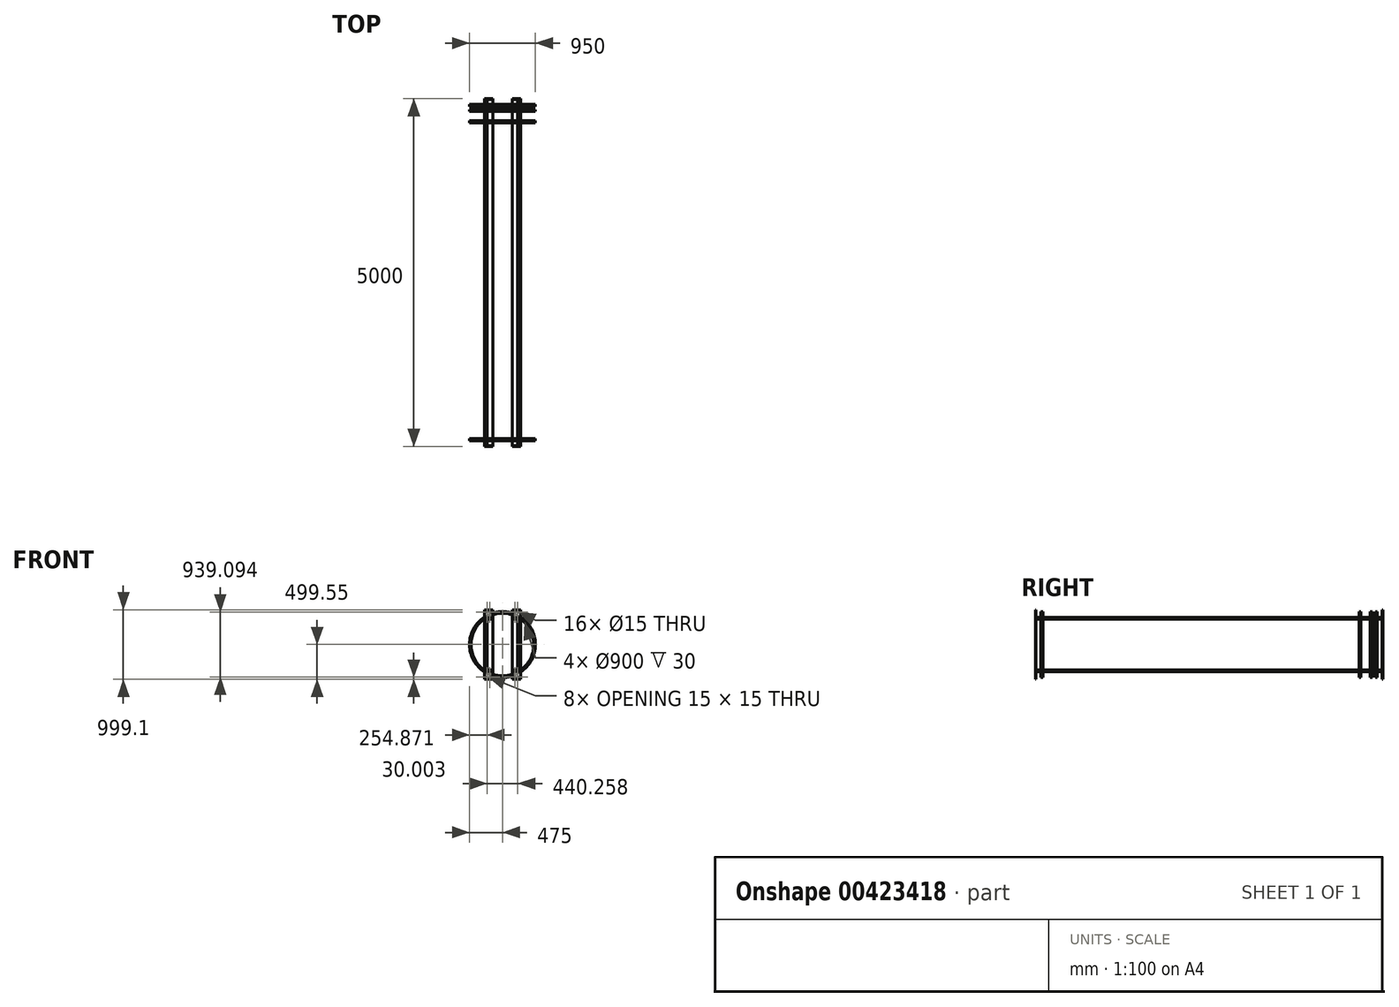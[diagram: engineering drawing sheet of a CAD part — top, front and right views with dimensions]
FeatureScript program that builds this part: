
annotation { "Feature Type Name" : "Feature", "Feature Type Description" : "" }
export const myFeature = defineFeature(function(context is Context, id is Id, definition is map)
    precondition{}
    {
        {
            var Q0;
            Q0=qCreatedBy(makeId("Front.planeOp"),FACE);
            var sketch = newSketch(context, id + "F0", { "sketchPlane" : qUnion([Q0])});
            skCircle(sketch, "E0", {"center": v(0, 0) * mm, "radius": 450 * mm, "construction": true});
            skLineSegment(sketch, "E1", {"start": v(0, 0) * mm, "end": v(0, 450) * mm, "construction": true});
            skLineSegment(sketch, "E2", {"start": v(0, 0) * mm, "end": v(-450, 0) * mm, "construction": true});
            skPoint(sketch, "E3", {"position": v(-236, 0) * mm});
            skPoint(sketch, "E4", {"position": v(-220, 0) * mm});
            skLineSegment(sketch, "E5", {"start": v(-236, 383.15) * mm, "end": v(-236, -383.15) * mm});
            skLineSegment(sketch, "E6", {"start": v(-220, 392.56) * mm, "end": v(-220, -392.56) * mm});
            skArc(sketch, "E7", {"start": v(-220, -392.56) * mm, "mid": v(-228.05, -387.94) * mm, "end": v(-236, -383.15) * mm});
            skLineSegment(sketch, "E8", {"start": v(-220, 383.15) * mm, "end": v(-140, 383.15) * mm});
            skLineSegment(sketch, "E9", {"start": v(-140, 383.15) * mm, "end": v(-140, 367.15) * mm});
            skLineSegment(sketch, "E10", {"start": v(-140, 367.15) * mm, "end": v(-220, 367.15) * mm});
            skLineSegment(sketch, "E11", {"start": v(-220, -383.15) * mm, "end": v(-140, -383.15) * mm});
            skLineSegment(sketch, "E12", {"start": v(-140, -383.15) * mm, "end": v(-140, -367.15) * mm});
            skLineSegment(sketch, "E13", {"start": v(-140, -367.15) * mm, "end": v(-220, -367.15) * mm});
            skPoint(sketch, "E14", {"position": v(-236, 383.15) * mm});
            skPoint(sketch, "E15", {"position": v(-220, 392.56) * mm});
            skLineSegment(sketch, "E16", {"start": v(-236, 367.15) * mm, "end": v(-260.2, 367.15) * mm});
            skArc(sketch, "E17", {"start": v(-220, 392.56) * mm, "mid": v(-240.43, 380.38) * mm, "end": v(-260.2, 367.15) * mm});
            skLineSegment(sketch, "E18", {"start": v(-236, -367.15) * mm, "end": v(-260.2, -367.15) * mm});
            skArc(sketch, "E19", {"start": v(-260.2, -367.15) * mm, "mid": v(-240.43, -380.38) * mm, "end": v(-220, -392.56) * mm});
            skArc(sketch, "E20.MirrorCS", {"start": v(220, -392.56) * mm, "mid": v(228.05, -387.94) * mm, "end": v(236, -383.15) * mm});
            skArc(sketch, "E21.MirrorCS", {"start": v(220, 392.56) * mm, "mid": v(240.43, 380.38) * mm, "end": v(260.2, 367.15) * mm});
            skLineSegment(sketch, "E22.MirrorCS", {"start": v(236, -367.15) * mm, "end": v(260.2, -367.15) * mm});
            skArc(sketch, "E23.MirrorCS", {"start": v(260.2, -367.15) * mm, "mid": v(240.43, -380.38) * mm, "end": v(220, -392.56) * mm});
            skLineSegment(sketch, "E24.MirrorCS", {"start": v(140, 383.15) * mm, "end": v(140, 367.15) * mm});
            skLineSegment(sketch, "E25.MirrorCS", {"start": v(140, -383.15) * mm, "end": v(140, -367.15) * mm});
            skLineSegment(sketch, "E26.MirrorCS", {"start": v(236, 367.15) * mm, "end": v(260.2, 367.15) * mm});
            skLineSegment(sketch, "E27.MirrorCS", {"start": v(236, 383.15) * mm, "end": v(236, -383.15) * mm});
            skPoint(sketch, "E28.MirrorP", {"position": v(220, 392.56) * mm});
            skLineSegment(sketch, "E29.MirrorCS", {"start": v(220, 392.56) * mm, "end": v(220, -392.56) * mm});
            skPoint(sketch, "E30.MirrorP", {"position": v(236, 0) * mm});
            skPoint(sketch, "E31.MirrorP", {"position": v(236, 383.15) * mm});
            skLineSegment(sketch, "E32.MirrorCS", {"start": v(220, -383.15) * mm, "end": v(140, -383.15) * mm});
            skLineSegment(sketch, "E33.MirrorCS", {"start": v(220, 383.15) * mm, "end": v(140, 383.15) * mm});
            skPoint(sketch, "E34.MirrorP", {"position": v(220, 0) * mm});
            skLineSegment(sketch, "E35.MirrorCS", {"start": v(140, -367.15) * mm, "end": v(220, -367.15) * mm});
            skLineSegment(sketch, "E36.MirrorCS", {"start": v(140, 367.15) * mm, "end": v(220, 367.15) * mm});
            skSolve(sketch);
        }
        {
            var Q0;
            Q0=makeQuery(id+"F0.imprint","IMPRINT",FACE,{"disambiguationData":[TD([[makeQuery(id+"F0.imprint","IMPRINT",EDGE,{"derivedFrom":sQuery(id+"F0.wireOp",EDGE,"E5")}),1.0]])]});
            var Q1;
            Q1=makeQuery(id+"F0.imprint","IMPRINT",FACE,{"disambiguationData":[TD([[makeQuery(id+"F0.imprint","IMPRINT",EDGE,{"derivedFrom":sQuery(id+"F0.wireOp",EDGE,"2efd4ff9-453e-46e9-b396-3085977d25950.MirrorCS")}),1.0]])]});
            var Q2;
            {var subQ3=sQuery(id+"F0.wireOp",EDGE,"E16");Q2=makeQuery(id+"F0.imprint","IMPRINT",FACE,{"disambiguationData":[TD([[makeQuery(id+"F0.imprint","IMPRINT",EDGE,{"derivedFrom":subQ3}),-1.0]])]});}
            var Q3;
            {var subQ0=sQuery(id+"F0.wireOp",EDGE,"E8");Q3=makeQuery(id+"F0.imprint","IMPRINT",FACE,{"disambiguationData":[TD([[makeQuery(id+"F0.imprint","IMPRINT",EDGE,{"derivedFrom":subQ0}),-1.0]])]});}
            var Q4;
            Q4=makeQuery(id+"F0.imprint","IMPRINT",FACE,{"disambiguationData":[TD([[makeQuery(id+"F0.imprint","IMPRINT",EDGE,{"derivedFrom":sQuery(id+"F0.wireOp",EDGE,"E24.MirrorCS")}),1.0]])]});
            var Q5;
            {var subQ0=sQuery(id+"F0.wireOp",EDGE,"E26.MirrorCS");Q5=makeQuery(id+"F0.imprint","IMPRINT",FACE,{"disambiguationData":[TD([[makeQuery(id+"F0.imprint","IMPRINT",EDGE,{"derivedFrom":subQ0}),1.0]])]});}
            var Q6;
            {var subQ2=sQuery(id+"F0.wireOp",EDGE,"E21.MirrorCS");var subQ5=sQuery(id+"F0.wireOp",EDGE,"E29.MirrorCS");var subQ10=makeQuery(id+"F0.imprint","INTERSECT",VERTEX,{"derivedFrom":[subQ2,subQ5]});Q6=makeQuery(id+"F0.imprint","IMPRINT",FACE,{"disambiguationData":[TD([[makeQuery(id+"F0.imprint","IMPRINT",EDGE,{"disambiguationData":[TD([[subQ10,-1.0]])],"derivedFrom":subQ2}),-1.0]])]});}
            var Q7;
            {var subQ0=sQuery(id+"F0.wireOp",EDGE,"E22.MirrorCS");Q7=makeQuery(id+"F0.imprint","IMPRINT",FACE,{"disambiguationData":[TD([[makeQuery(id+"F0.imprint","IMPRINT",EDGE,{"derivedFrom":subQ0}),-1.0]])]});}
            var Q8;
            Q8=makeQuery(id+"F0.imprint","IMPRINT",FACE,{"disambiguationData":[TD([[makeQuery(id+"F0.imprint","IMPRINT",EDGE,{"derivedFrom":sQuery(id+"F0.wireOp",EDGE,"E25.MirrorCS")}),-1.0]])]});
            var Q9;
            {var subQ0=sQuery(id+"F0.wireOp",EDGE,"E11");Q9=makeQuery(id+"F0.imprint","IMPRINT",FACE,{"disambiguationData":[TD([[makeQuery(id+"F0.imprint","IMPRINT",EDGE,{"derivedFrom":subQ0}),1.0]])]});}
            var Q10;
            {var subQ3=sQuery(id+"F0.wireOp",EDGE,"E18");Q10=makeQuery(id+"F0.imprint","IMPRINT",FACE,{"disambiguationData":[TD([[makeQuery(id+"F0.imprint","IMPRINT",EDGE,{"derivedFrom":subQ3}),1.0]])]});}
            extrude(context, id + "F1", {"entities" : qUnion([Q0, Q1, Q2, Q3, Q4, Q5, Q6, Q7, Q8, Q9, Q10]), "depth" : 5000 * mm});
        }
        {
            var Q0;
            Q0=qCreatedBy(makeId("Front.planeOp"),FACE);
            cPlane(context, id + "F2", {"entities" : qUnion([Q0]), "cplaneType" : CPlaneType.OFFSET, "offset" : 80 * mm, "width" : 150 * mm, "height" : 150 * mm});
        }
        {
            var Q0;
            Q0=qCreatedBy(makeId("Front.planeOp"),FACE);
            cPlane(context, id + "F3", {"entities" : qUnion([Q0]), "cplaneType" : CPlaneType.OFFSET, "offset" : ((484 / 3) + 8) * mm, "width" : 150 * mm, "height" : 150 * mm});
        }
        {
            var Q0;
            Q0=qCreatedBy(makeId("Front.planeOp"),FACE);
            cPlane(context, id + "F4", {"entities" : qUnion([Q0]), "cplaneType" : CPlaneType.OFFSET, "offset" : ((484 / 3) + (484 / 3) + 8) * mm, "width" : 150 * mm, "height" : 150 * mm});
        }
        {
            var Q0;
            Q0=qCreatedBy(makeId("Front.planeOp"),FACE);
            cPlane(context, id + "F5", {"entities" : qUnion([Q0]), "cplaneType" : CPlaneType.OFFSET, "offset" : 4920 * mm, "width" : 150 * mm, "height" : 150 * mm});
        }
        {
            var Q0;
            Q0=qCreatedBy(id+"F2.planeOp",FACE);
            var sketch = newSketch(context, id + "F6", { "sketchPlane" : qUnion([Q0])});
            skCircle(sketch, "E37", {"center": v(0, 0) * mm, "radius": 450 * mm});
            skCircle(sketch, "E38", {"center": v(0, 0) * mm, "radius": 475 * mm});
            skSolve(sketch);
        }
        {
            var Q0;
            Q0=qCreatedBy(id+"F3.planeOp",FACE);
            var sketch = newSketch(context, id + "F7", { "sketchPlane" : qUnion([Q0])});
            skCircle(sketch, "E39", {"center": v(0, 0) * mm, "radius": 450 * mm});
            skCircle(sketch, "E40", {"center": v(0, 0) * mm, "radius": 475 * mm});
            skSolve(sketch);
        }
        {
            var Q0;
            Q0=qCreatedBy(id+"F4.planeOp",FACE);
            var sketch = newSketch(context, id + "F8", { "sketchPlane" : qUnion([Q0])});
            skCircle(sketch, "E41", {"center": v(0, 0) * mm, "radius": 450 * mm});
            skCircle(sketch, "E42", {"center": v(0, 0) * mm, "radius": 475 * mm});
            skSolve(sketch);
        }
        {
            var Q0;
            Q0=qCreatedBy(id+"F5.planeOp",FACE);
            var sketch = newSketch(context, id + "F9", { "sketchPlane" : qUnion([Q0])});
            skCircle(sketch, "E43", {"center": v(0, 0) * mm, "radius": 450 * mm});
            skCircle(sketch, "E44", {"center": v(0, 0) * mm, "radius": 475 * mm});
            skSolve(sketch);
        }
        {
            var Q0;
            Q0 = qSketchRegion(id + "F6", true);
            extrude(context, id + "F10", {"entities" : qUnion([Q0]), "depth" : 30 * mm});
        }
        {
            var Q0;
            Q0=makeQuery(id+"F7.imprint","IMPRINT",FACE,{"disambiguationData":[TD([[makeQuery(id+"F7.imprint","IMPRINT",EDGE,{"derivedFrom":sQuery(id+"F7.wireOp",EDGE,"E39")}),-1.0]])]});
            extrude(context, id + "F11", {"entities" : qUnion([Q0]), "depth" : 15 * mm, "hasSecondDirection" : true, "secondDirectionOppositeDirection" : true, "secondDirectionDepth" : 15 * mm});
        }
        {
            var Q0;
            Q0 = qSketchRegion(id + "F9", true);
            extrude(context, id + "F12", {"entities" : qUnion([Q0]), "oppositeDirection" : true, "depth" : 30 * mm});
        }
        {
            var Q0;
            Q0=makeQuery(id+"F8.imprint","IMPRINT",FACE,{"disambiguationData":[TD([[makeQuery(id+"F8.imprint","IMPRINT",EDGE,{"derivedFrom":sQuery(id+"F8.wireOp",EDGE,"E41")}),-1.0]])]});
            extrude(context, id + "F13", {"entities" : qUnion([Q0]), "depth" : 15 * mm, "hasSecondDirection" : true, "secondDirectionOppositeDirection" : true, "secondDirectionDepth" : 15 * mm});
        }
        {
            var Q0;
            Q0=qCreatedBy(id+"F2.planeOp",FACE);
            var sketch = newSketch(context, id + "F14", { "sketchPlane" : qUnion([Q0])});
            skCircle(sketch, "E45", {"center": v(0, 0) * mm, "radius": 450 * mm});
            skSolve(sketch);
        }
        {
            var Q0;
            Q0=qCreatedBy(id+"F5.planeOp",FACE);
            var sketch = newSketch(context, id + "F15", { "sketchPlane" : qUnion([Q0])});
            skCircle(sketch, "E46", {"center": v(0, 0) * mm, "radius": 450 * mm});
            skSolve(sketch);
        }
        {
            var Q0;
            Q0 = qSketchRegion(id + "F14", true);
            extrude(context, id + "F16", {"entities" : qUnion([Q0]), "depth" : 10 * mm});
        }
        {
            var Q0;
            Q0 = qSketchRegion(id + "F15", true);
            extrude(context, id + "F17", {"entities" : qUnion([Q0]), "oppositeDirection" : true, "depth" : 10 * mm});
        }
        {
            var Q0;
            Q0=qCreatedBy(makeId("Front.planeOp"),FACE);
            var sketch = newSketch(context, id + "F18", { "sketchPlane" : qUnion([Q0])});
            skCircle(sketch, "E47", {"center": v(0, 0) * mm, "radius": 450 * mm, "construction": true});
            skLineSegment(sketch, "E48", {"start": v(0, 0) * mm, "end": v(0, 450) * mm, "construction": true});
            skLineSegment(sketch, "E49", {"start": v(0, 0) * mm, "end": v(-450, 0) * mm, "construction": true});
            skPoint(sketch, "E50", {"position": v(-236, 0) * mm});
            skPoint(sketch, "E51", {"position": v(-220, 0) * mm});
            skLineSegment(sketch, "E52", {"start": v(-236, 383.15) * mm, "end": v(-236, -383.15) * mm});
            skLineSegment(sketch, "E53", {"start": v(-220, 392.56) * mm, "end": v(-220, -392.56) * mm});
            skArc(sketch, "E54", {"start": v(-220, -392.56) * mm, "mid": v(-228.05, -387.94) * mm, "end": v(-236, -383.15) * mm});
            skLineSegment(sketch, "E55", {"start": v(-220, 383.15) * mm, "end": v(-140, 383.15) * mm});
            skLineSegment(sketch, "E56", {"start": v(-140, 383.15) * mm, "end": v(-140, 367.15) * mm});
            skLineSegment(sketch, "E57", {"start": v(-140, 367.15) * mm, "end": v(-220, 367.15) * mm});
            skLineSegment(sketch, "E58", {"start": v(-220, -383.15) * mm, "end": v(-140, -383.15) * mm});
            skLineSegment(sketch, "E59", {"start": v(-140, -383.15) * mm, "end": v(-140, -367.15) * mm});
            skLineSegment(sketch, "E60", {"start": v(-140, -367.15) * mm, "end": v(-220, -367.15) * mm});
            skPoint(sketch, "E61", {"position": v(-236, 383.15) * mm});
            skPoint(sketch, "E62", {"position": v(-220, 392.56) * mm});
            skLineSegment(sketch, "E63", {"start": v(-236, 367.15) * mm, "end": v(-260.2, 367.15) * mm});
            skArc(sketch, "E64", {"start": v(-220, 392.56) * mm, "mid": v(-240.43, 380.38) * mm, "end": v(-260.2, 367.15) * mm});
            skLineSegment(sketch, "E65", {"start": v(-236, -367.15) * mm, "end": v(-260.2, -367.15) * mm});
            skArc(sketch, "E66", {"start": v(-260.2, -367.15) * mm, "mid": v(-240.43, -380.38) * mm, "end": v(-220, -392.56) * mm});
            skArc(sketch, "E67.MirrorCS", {"start": v(220, -392.56) * mm, "mid": v(228.05, -387.94) * mm, "end": v(236, -383.15) * mm});
            skArc(sketch, "E68.MirrorCS", {"start": v(220, 392.56) * mm, "mid": v(240.43, 380.38) * mm, "end": v(260.2, 367.15) * mm});
            skLineSegment(sketch, "E69.MirrorCS", {"start": v(236, -367.15) * mm, "end": v(260.2, -367.15) * mm});
            skArc(sketch, "E70.MirrorCS", {"start": v(260.2, -367.15) * mm, "mid": v(240.43, -380.38) * mm, "end": v(220, -392.56) * mm});
            skLineSegment(sketch, "E71.MirrorCS", {"start": v(140, 383.15) * mm, "end": v(140, 367.15) * mm});
            skLineSegment(sketch, "E72.MirrorCS", {"start": v(140, -383.15) * mm, "end": v(140, -367.15) * mm});
            skLineSegment(sketch, "E73.MirrorCS", {"start": v(236, 367.15) * mm, "end": v(260.2, 367.15) * mm});
            skLineSegment(sketch, "E74.MirrorCS", {"start": v(236, 383.15) * mm, "end": v(236, -383.15) * mm});
            skPoint(sketch, "E75.MirrorP", {"position": v(220, 392.56) * mm});
            skLineSegment(sketch, "E76.MirrorCS", {"start": v(220, 392.56) * mm, "end": v(220, -392.56) * mm});
            skPoint(sketch, "E77.MirrorP", {"position": v(236, 0) * mm});
            skPoint(sketch, "E78.MirrorP", {"position": v(236, 383.15) * mm});
            skLineSegment(sketch, "E79.MirrorCS", {"start": v(220, -383.15) * mm, "end": v(140, -383.15) * mm});
            skLineSegment(sketch, "E80.MirrorCS", {"start": v(220, 383.15) * mm, "end": v(140, 383.15) * mm});
            skPoint(sketch, "E81.MirrorP", {"position": v(220, 0) * mm});
            skLineSegment(sketch, "E82.MirrorCS", {"start": v(140, -367.15) * mm, "end": v(220, -367.15) * mm});
            skLineSegment(sketch, "E83.MirrorCS", {"start": v(140, 367.15) * mm, "end": v(220, 367.15) * mm});
            skLineSegment(sketch, "E84", {"start": v(140, 383.15) * mm, "end": v(140, 499.55) * mm});
            skLineSegment(sketch, "E85", {"start": v(140, 499.55) * mm, "end": v(260.2, 499.55) * mm});
            skLineSegment(sketch, "E86", {"start": v(260.2, 499.55) * mm, "end": v(260.2, 367.15) * mm});
            skLineSegment(sketch, "E87", {"start": v(140, 367.15) * mm, "end": v(140, -367.15) * mm});
            skLineSegment(sketch, "E88", {"start": v(260.2, 367.15) * mm, "end": v(260.2, -367.15) * mm});
            skCircle(sketch, "E89", {"center": v(0, 0) * mm, "radius": 475 * mm, "construction": true});
            skPoint(sketch, "E90", {"position": v(140, 453.9) * mm});
            skPoint(sketch, "E91", {"position": v(140, 469.55) * mm});
            skPoint(sketch, "E92", {"position": v(180.06, 469.55) * mm});
            skPoint(sketch, "E93", {"position": v(220.13, 469.55) * mm});
            skPoint(sketch, "E94", {"position": v(260.2, 469.55) * mm});
            skLineSegment(sketch, "E95.MirrorCS", {"start": v(-260.2, 499.55) * mm, "end": v(-260.2, 367.15) * mm});
            skLineSegment(sketch, "E96.MirrorCS", {"start": v(-140, 383.15) * mm, "end": v(-140, 499.55) * mm});
            skLineSegment(sketch, "E97.MirrorCS", {"start": v(-140, 499.55) * mm, "end": v(-260.2, 499.55) * mm});
            skPoint(sketch, "E98.MirrorP", {"position": v(-180.06, 469.55) * mm});
            skPoint(sketch, "E99.MirrorP", {"position": v(-140, 469.55) * mm});
            skPoint(sketch, "E100.MirrorP", {"position": v(-260.2, 469.55) * mm});
            skPoint(sketch, "E101.MirrorP", {"position": v(-140, 453.9) * mm});
            skPoint(sketch, "E102.MirrorP", {"position": v(-220.13, 469.55) * mm});
            skLineSegment(sketch, "E103.MirrorCS", {"start": v(260.2, -499.55) * mm, "end": v(260.2, -367.15) * mm});
            skLineSegment(sketch, "E104.MirrorCS", {"start": v(-260.2, -499.55) * mm, "end": v(-260.2, -367.15) * mm});
            skPoint(sketch, "E105.MirrorP", {"position": v(-220, -392.56) * mm});
            skPoint(sketch, "E106.MirrorP", {"position": v(-236, -383.15) * mm});
            skPoint(sketch, "E107.MirrorP", {"position": v(-180.06, -469.55) * mm});
            skPoint(sketch, "E108.MirrorP", {"position": v(-220.13, -469.55) * mm});
            skLineSegment(sketch, "E109.MirrorCS", {"start": v(140, -499.55) * mm, "end": v(260.2, -499.55) * mm});
            skPoint(sketch, "E110.MirrorP", {"position": v(236, -383.15) * mm});
            skPoint(sketch, "E111.MirrorP", {"position": v(-140, -469.55) * mm});
            skLineSegment(sketch, "E112.MirrorCS", {"start": v(-140, -383.15) * mm, "end": v(-140, -499.55) * mm});
            skPoint(sketch, "E113.MirrorP", {"position": v(-140, -453.9) * mm});
            skPoint(sketch, "E114.MirrorP", {"position": v(180.06, -469.55) * mm});
            skPoint(sketch, "E115.MirrorP", {"position": v(220.13, -469.55) * mm});
            skLineSegment(sketch, "E116.MirrorCS", {"start": v(140, -383.15) * mm, "end": v(140, -499.55) * mm});
            skLineSegment(sketch, "E117.MirrorCS", {"start": v(-140, -499.55) * mm, "end": v(-260.2, -499.55) * mm});
            skPoint(sketch, "E118.MirrorP", {"position": v(-260.2, -469.55) * mm});
            skPoint(sketch, "E119.MirrorP", {"position": v(140, -453.9) * mm});
            skPoint(sketch, "E120.MirrorP", {"position": v(220, -392.56) * mm});
            skPoint(sketch, "E121.MirrorP", {"position": v(140, -469.55) * mm});
            skPoint(sketch, "E122.MirrorP", {"position": v(260.2, -469.55) * mm});
            skLineSegment(sketch, "E123", {"start": v(-140, 367.15) * mm, "end": v(-140, -367.15) * mm});
            skLineSegment(sketch, "E124", {"start": v(-260.2, 367.15) * mm, "end": v(-260.2, -367.15) * mm});
            skPoint(sketch, "E125", {"position": v(180.06, 439.55) * mm});
            skSolve(sketch);
        }
        {
            var Q0;
            {var subQ0=sQuery(id+"F18.wireOp",EDGE,"E80.MirrorCS");Q0=makeQuery(id+"F18.imprint","IMPRINT",FACE,{"disambiguationData":[TD([[makeQuery(id+"F18.imprint","IMPRINT",EDGE,{"derivedFrom":subQ0}),-1.0]])]});}
            var Q1;
            {var subQ0=sQuery(id+"F18.wireOp",EDGE,"E95.MirrorCS");Q1=makeQuery(id+"F18.imprint","IMPRINT",FACE,{"disambiguationData":[TD([[makeQuery(id+"F18.imprint","IMPRINT",EDGE,{"derivedFrom":subQ0}),1.0]])]});}
            var Q2;
            {var subQ2=sQuery(id+"F18.wireOp",EDGE,"E104.MirrorCS");Q2=makeQuery(id+"F18.imprint","IMPRINT",FACE,{"disambiguationData":[TD([[makeQuery(id+"F18.imprint","IMPRINT",EDGE,{"derivedFrom":subQ2}),-1.0]])]});}
            var Q3;
            {var subQ5=sQuery(id+"F18.wireOp",EDGE,"E103.MirrorCS");Q3=makeQuery(id+"F18.imprint","IMPRINT",FACE,{"disambiguationData":[TD([[makeQuery(id+"F18.imprint","IMPRINT",EDGE,{"derivedFrom":subQ5}),1.0]])]});}
            var Q4;
            {var subQ0=sQuery(id+"F18.wireOp",EDGE,"E82.MirrorCS");Q4=makeQuery(id+"F18.imprint","IMPRINT",FACE,{"disambiguationData":[TD([[makeQuery(id+"F18.imprint","IMPRINT",EDGE,{"derivedFrom":subQ0}),1.0]])]});}
            var Q5;
            {var subQ0=sQuery(id+"F18.wireOp",EDGE,"E69.MirrorCS");Q5=makeQuery(id+"F18.imprint","IMPRINT",FACE,{"disambiguationData":[TD([[makeQuery(id+"F18.imprint","IMPRINT",EDGE,{"derivedFrom":subQ0}),1.0]])]});}
            var Q6;
            {var subQ0=sQuery(id+"F18.wireOp",EDGE,"E57");Q6=makeQuery(id+"F18.imprint","IMPRINT",FACE,{"disambiguationData":[TD([[makeQuery(id+"F18.imprint","IMPRINT",EDGE,{"derivedFrom":subQ0}),1.0]])]});}
            var Q7;
            {var subQ0=sQuery(id+"F18.wireOp",EDGE,"E63");Q7=makeQuery(id+"F18.imprint","IMPRINT",FACE,{"disambiguationData":[TD([[makeQuery(id+"F18.imprint","IMPRINT",EDGE,{"derivedFrom":subQ0}),1.0]])]});}
            extrude(context, id + "F19", {"entities" : qUnion([Q0, Q1, Q2, Q3, Q4, Q5, Q6, Q7]), "depth" : 11 * mm});
        }
        {
            var Q0;
            Q0=sQuery(id+"F18.wireOp",VERTEX,"E102.MirrorP");
            var Q1;
            Q1=sQuery(id+"F18.wireOp",VERTEX,"E98.MirrorP");
            var Q2;
            Q2=sQuery(id+"F18.wireOp",VERTEX,"E92");
            var Q3;
            Q3=sQuery(id+"F18.wireOp",VERTEX,"E93");
            var Q4;
            Q4=sQuery(id+"F18.wireOp",VERTEX,"E108.MirrorP");
            var Q5;
            Q5=sQuery(id+"F18.wireOp",VERTEX,"E107.MirrorP");
            var Q6;
            Q6=sQuery(id+"F18.wireOp",VERTEX,"E114.MirrorP");
            var Q7;
            Q7=sQuery(id+"F18.wireOp",VERTEX,"E115.MirrorP");
            var Q8;
            Q8=makeQuery(id+"F19.opExtrude","SWEPT_BODY",BODY,{"disambiguationData":[OSD([sQuery(id+"F18.wireOp",EDGE,"E53"),sQuery(id+"F18.wireOp",EDGE,"E64"),sQuery(id+"F18.wireOp",EDGE,"E95.MirrorCS"),sQuery(id+"F18.wireOp",EDGE,"E96.MirrorCS"),sQuery(id+"F18.wireOp",EDGE,"E97.MirrorCS"),sQuery(id+"F18.wireOp",EDGE,"E55")])]});
            var Q9;
            Q9=makeQuery(id+"F19.opExtrude","SWEPT_BODY",BODY,{"disambiguationData":[OSD([sQuery(id+"F18.wireOp",EDGE,"E68.MirrorCS"),sQuery(id+"F18.wireOp",EDGE,"E76.MirrorCS"),sQuery(id+"F18.wireOp",EDGE,"E80.MirrorCS"),sQuery(id+"F18.wireOp",EDGE,"E84"),sQuery(id+"F18.wireOp",EDGE,"E85"),sQuery(id+"F18.wireOp",EDGE,"E86")])]});
            var Q10;
            Q10=makeQuery(id+"F19.opExtrude","SWEPT_BODY",BODY,{"disambiguationData":[OSD([sQuery(id+"F18.wireOp",EDGE,"E53"),sQuery(id+"F18.wireOp",EDGE,"E66"),sQuery(id+"F18.wireOp",EDGE,"E104.MirrorCS"),sQuery(id+"F18.wireOp",EDGE,"E112.MirrorCS"),sQuery(id+"F18.wireOp",EDGE,"E58"),sQuery(id+"F18.wireOp",EDGE,"E117.MirrorCS")])]});
            var Q11;
            Q11=makeQuery(id+"F19.opExtrude","SWEPT_BODY",BODY,{"disambiguationData":[OSD([sQuery(id+"F18.wireOp",EDGE,"E70.MirrorCS"),sQuery(id+"F18.wireOp",EDGE,"E76.MirrorCS"),sQuery(id+"F18.wireOp",EDGE,"E103.MirrorCS"),sQuery(id+"F18.wireOp",EDGE,"E109.MirrorCS"),sQuery(id+"F18.wireOp",EDGE,"E79.MirrorCS"),sQuery(id+"F18.wireOp",EDGE,"E116.MirrorCS")])]});
            hole(context, id + "F20", {"style" : HoleStyle.SIMPLE, "endStyle" : HoleEndStyle.THROUGH, "oppositeDirection" : true, "holeDiameter" : 15 * mm, "isTappedThrough" : true, "tappedDepth" : 12 * mm, "tapClearance" : 3, "locations" : qUnion([Q0, Q1, Q2, Q3, Q4, Q5, Q6, Q7]), "scope" : qUnion([Q8, Q9, Q10, Q11])});
        }
        {
            var Q0;
            Q0=qCreatedBy(makeId("Front.planeOp"),FACE);
            cPlane(context, id + "F21", {"entities" : qUnion([Q0]), "cplaneType" : CPlaneType.OFFSET, "offset" : 2500 * mm, "width" : 150 * mm, "height" : 150 * mm});
        }
        {
            var Q0;
            Q0=makeQuery(id+"F1.opExtrude","SWEPT_BODY",BODY,{"disambiguationData":[OSD([sQuery(id+"F0.wireOp",EDGE,"E21.MirrorCS"),sQuery(id+"F0.wireOp",EDGE,"E22.MirrorCS"),sQuery(id+"F0.wireOp",EDGE,"E23.MirrorCS"),sQuery(id+"F0.wireOp",EDGE,"E24.MirrorCS"),sQuery(id+"F0.wireOp",EDGE,"E25.MirrorCS"),sQuery(id+"F0.wireOp",EDGE,"E26.MirrorCS"),sQuery(id+"F0.wireOp",EDGE,"E27.MirrorCS"),sQuery(id+"F0.wireOp",EDGE,"E29.MirrorCS"),sQuery(id+"F0.wireOp",EDGE,"E32.MirrorCS"),sQuery(id+"F0.wireOp",EDGE,"E33.MirrorCS"),sQuery(id+"F0.wireOp",EDGE,"E35.MirrorCS"),sQuery(id+"F0.wireOp",EDGE,"E36.MirrorCS")])]});
            var Q1;
            Q1=makeQuery(id+"F19.opExtrude","SWEPT_BODY",BODY,{"disambiguationData":[OSD([sQuery(id+"F18.wireOp",EDGE,"E68.MirrorCS"),sQuery(id+"F18.wireOp",EDGE,"E76.MirrorCS"),sQuery(id+"F18.wireOp",EDGE,"E80.MirrorCS"),sQuery(id+"F18.wireOp",EDGE,"E84"),sQuery(id+"F18.wireOp",EDGE,"E85"),sQuery(id+"F18.wireOp",EDGE,"E86")])]});
            var Q2;
            Q2=makeQuery(id+"F19.opExtrude","SWEPT_BODY",BODY,{"disambiguationData":[OSD([sQuery(id+"F18.wireOp",EDGE,"E70.MirrorCS"),sQuery(id+"F18.wireOp",EDGE,"E76.MirrorCS"),sQuery(id+"F18.wireOp",EDGE,"E103.MirrorCS"),sQuery(id+"F18.wireOp",EDGE,"E109.MirrorCS"),sQuery(id+"F18.wireOp",EDGE,"E79.MirrorCS"),sQuery(id+"F18.wireOp",EDGE,"E116.MirrorCS")])]});
            var Q3;
            Q3=makeQuery(id+"F19.opExtrude","SWEPT_BODY",BODY,{"disambiguationData":[OSD([sQuery(id+"F18.wireOp",EDGE,"E69.MirrorCS"),sQuery(id+"F18.wireOp",EDGE,"E73.MirrorCS"),sQuery(id+"F18.wireOp",EDGE,"E74.MirrorCS"),sQuery(id+"F18.wireOp",EDGE,"E88")])]});
            var Q4;
            Q4=makeQuery(id+"F19.opExtrude","SWEPT_BODY",BODY,{"disambiguationData":[OSD([sQuery(id+"F18.wireOp",EDGE,"E53"),sQuery(id+"F18.wireOp",EDGE,"E64"),sQuery(id+"F18.wireOp",EDGE,"E95.MirrorCS"),sQuery(id+"F18.wireOp",EDGE,"E96.MirrorCS"),sQuery(id+"F18.wireOp",EDGE,"E97.MirrorCS"),sQuery(id+"F18.wireOp",EDGE,"E55")])]});
            var Q5;
            Q5=makeQuery(id+"F19.opExtrude","SWEPT_BODY",BODY,{"disambiguationData":[OSD([sQuery(id+"F18.wireOp",EDGE,"E53"),sQuery(id+"F18.wireOp",EDGE,"E66"),sQuery(id+"F18.wireOp",EDGE,"E104.MirrorCS"),sQuery(id+"F18.wireOp",EDGE,"E112.MirrorCS"),sQuery(id+"F18.wireOp",EDGE,"E58"),sQuery(id+"F18.wireOp",EDGE,"E117.MirrorCS")])]});
            var Q6;
            Q6=makeQuery(id+"F19.opExtrude","SWEPT_BODY",BODY,{"disambiguationData":[OSD([sQuery(id+"F18.wireOp",EDGE,"E76.MirrorCS"),sQuery(id+"F18.wireOp",EDGE,"E82.MirrorCS"),sQuery(id+"F18.wireOp",EDGE,"E83.MirrorCS"),sQuery(id+"F18.wireOp",EDGE,"E87")])]});
            var Q7;
            Q7=makeQuery(id+"F1.opExtrude","SWEPT_BODY",BODY,{"disambiguationData":[OSD([sQuery(id+"F0.wireOp",EDGE,"E5"),sQuery(id+"F0.wireOp",EDGE,"E6"),sQuery(id+"F0.wireOp",EDGE,"E8"),sQuery(id+"F0.wireOp",EDGE,"E9"),sQuery(id+"F0.wireOp",EDGE,"E10"),sQuery(id+"F0.wireOp",EDGE,"E11"),sQuery(id+"F0.wireOp",EDGE,"E12"),sQuery(id+"F0.wireOp",EDGE,"E13"),sQuery(id+"F0.wireOp",EDGE,"E16"),sQuery(id+"F0.wireOp",EDGE,"E17"),sQuery(id+"F0.wireOp",EDGE,"E18"),sQuery(id+"F0.wireOp",EDGE,"E19")])]});
            var Q8;
            Q8=makeQuery(id+"F19.opExtrude","SWEPT_BODY",BODY,{"disambiguationData":[OSD([sQuery(id+"F18.wireOp",EDGE,"E53"),sQuery(id+"F18.wireOp",EDGE,"E57"),sQuery(id+"F18.wireOp",EDGE,"E60"),sQuery(id+"F18.wireOp",EDGE,"E123")])]});
            var Q9;
            Q9=makeQuery(id+"F19.opExtrude","SWEPT_BODY",BODY,{"disambiguationData":[OSD([sQuery(id+"F18.wireOp",EDGE,"E52"),sQuery(id+"F18.wireOp",EDGE,"E63"),sQuery(id+"F18.wireOp",EDGE,"E65"),sQuery(id+"F18.wireOp",EDGE,"E124")])]});
            var Q10;
            Q10=qCreatedBy(id+"F21.planeOp",FACE);
            mirror(context, id + "F22", {"entities" : qUnion([Q0, Q1, Q2, Q3, Q4, Q5, Q6, Q7, Q8, Q9]), "mirrorPlane" : qUnion([Q10])});
        }
    });
